# Revit family: Haworth_Gambetta_SofaChair_TwoArm
name_source: partatom
category: Furniture
revit_build: Autodesk Revit 2018 (Build: 20170223_1515(x64)
units: mm (PartAtom-declared; Revit-internal decimal feet)

## family parameters
Always vertical = Yes
Cut with Voids When Loaded = No
OmniClass Number = 23.40.70.14.64.21
OmniClass Title = Systems Furniture
Room Calculation Point = No
Shared = No
Work Plane-Based = No

## types (2) — shared parameters
Actual Depth = 31 1/2"
Actual Height = 28 3/4"
Arm Offset = 4"
Assembly Code = E2020200
Base Finish = Haworth _ Paint _ Collection Black
Leg Offset = 2 1/4"
Manufacturer = Haworth
Model = HCCE-GBL
Revision Number = 1
Size = Verify Final Dim. w/ Haworth
URL = http://www.haworth.com
URL - Product = https://www.haworth.com
Warranty = http://www.haworth.com

## per-type parameters (varying)
| type | Actual Width | Chair | Cushion Width | Description | Two Seat Control | Two Seats |
| HCCE-GBL2-A - Two Seats Sofa | 63" | No | 27 1/2" | Haworth Gambetta Two Seats Sofa Two Arms | Yes | Yes |
| HCCE-GBL1-A - Lounge Chair | 29 1/2" | Yes | 21 1/2" | Haworth Gambetta Lounge Chair | No | No |

## geometry (parser evidence)
native form markers: Sweep x8
no freeform markers — native parametric forms only
